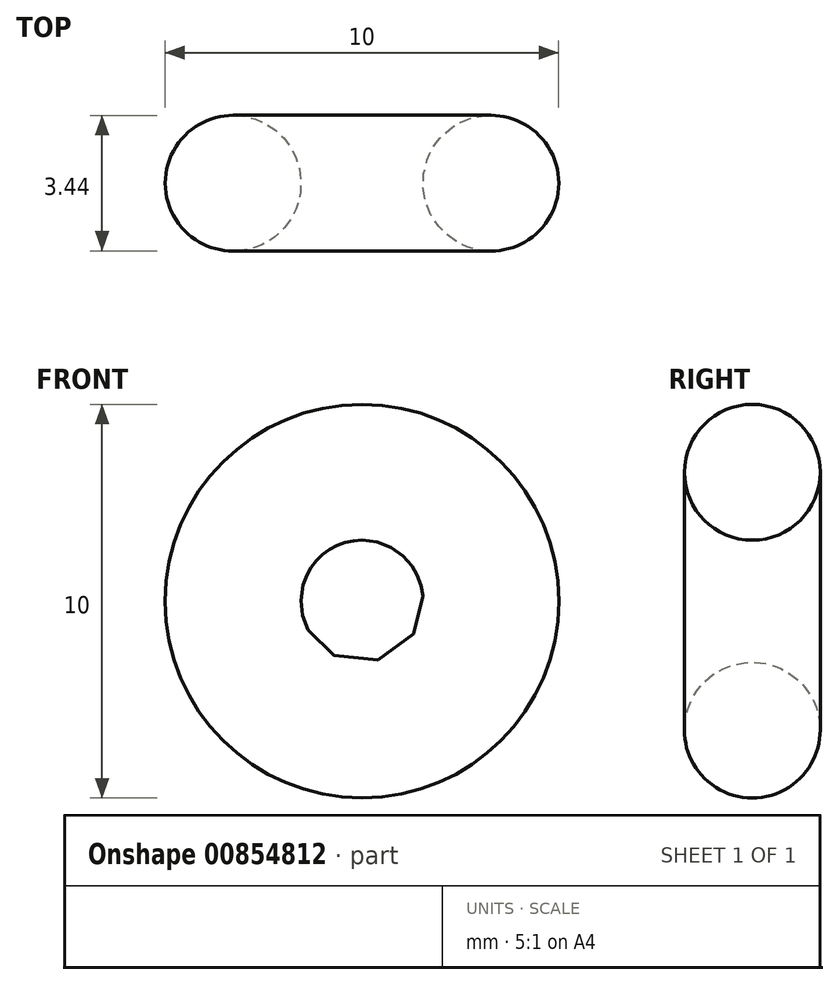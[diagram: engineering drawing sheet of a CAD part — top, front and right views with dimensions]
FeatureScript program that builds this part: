
annotation { "Feature Type Name" : "Feature", "Feature Type Description" : "" }
export const myFeature = defineFeature(function(context is Context, id is Id, definition is map)
    precondition{}
    {
        {
            var Q0;
            Q0=qCreatedBy(makeId("Top.planeOp"),FACE);
            var sketch = newSketch(context, id + "F0", { "sketchPlane" : qUnion([Q0])});
            skCircle(sketch, "E0", {"center": v(0, 0) * mm, "radius": 1.72 * mm});
            skLineSegment(sketch, "E1", {"start": v(-3.28, 1.9) * mm, "end": v(-3.28, -2.62) * mm});
            skSolve(sketch);
        }
        {
            var Q0;
            Q0=makeQuery(id+"F0.imprint","IMPRINT",FACE,{"disambiguationData":[TD([[makeQuery(id+"F0.imprint","IMPRINT",EDGE,{"derivedFrom":sQuery(id+"F0.wireOp",EDGE,"E0")}),1.0]])]});
            var Q1;
            Q1=sQuery(id+"F0.wireOp",EDGE,"E1");
            revolve(context, id + "F1", {"surfaceOperationType" : NewSurfaceOperationType.NEW, "entities" : qUnion([Q0]), "axis" : qUnion([Q1]), "revolveType" : RevolveType.FULL});
        }
    });
